# Revit family: Aeon
name_source: partatom
category: Мебель
revit_build: Autodesk Revit 2017 (Build: 20160225_1515(x64)
units: mm (PartAtom-declared; Revit-internal decimal feet)

## family parameters
Всегда вертикально = Да
Заголовок OmniClass = General Furniture and Specialties
На основе рабочей плоскости = Нет
Номер OmniClass = 23.40.20.00
Общий = Нет
При загрузке вырезать с полостями = Нет
Точка расчета площади = Нет

## types (3) — shared parameters
KS Seat = KS-Seat
Leg Material = Skandiform Chrome
Изготовитель = Skandiform AB
Ключевая пометка = XBF.2
Комментарии к типоразмеру = Created by Astacus AB

## per-type parameters (varying)
| type | Ks Legs | Seat Material | URL | Описание |
| KS-180 | KS-180 : Legs | Skandiform Fabric Red | http://file-system.ru | Armchair with swivelling pillar chassis on wheels |
| KS-181 | KS-181 : Legs | Skandiform Fabric Blue | http://www.biminfo.se | Armchair with swivelling pillar chassis on glides |
| KS-186 | KS-186 : Legs | Skandiform Fabric Red | http://www.biminfo.se | Armchair with chassis on metal runners |

note: column(s) folded — value = type name in every type: Группа модели

## geometry (parser evidence)
native form markers: Blend x25, Sweep x12
no freeform markers — native parametric forms only
